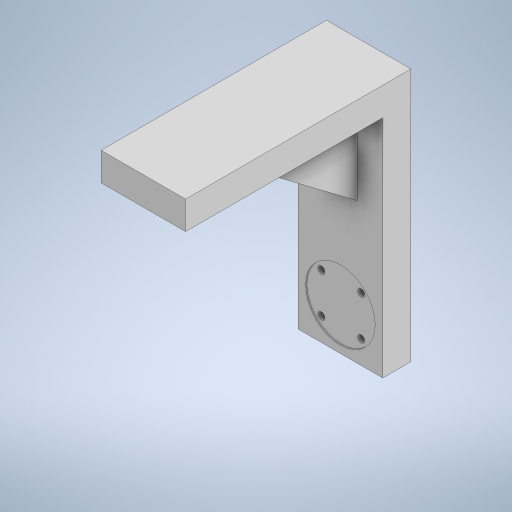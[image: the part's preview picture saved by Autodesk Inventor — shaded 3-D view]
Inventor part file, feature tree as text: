
AUTODESK INVENTOR PART (.ipt)
format: ipt  version: 2024 (Build 280153000, 153)  size: 284,160 bytes
history: native  units: in
note: dims shown in document units (in); Inventor stores cm internally (conversion verified against a paired STEP export)
features: sketch x7, extrude x6, rib x1
ambient origin geometry x8: Origin, YZ Plane, XZ Plane, XY Plane, X Axis, Y Axis, Z Axis, Center Point
bodies: Body1 (feature_tree)
feature tree (14):
  extrude  "Extrusion8"  Depth=1.9685in TaperAngle=0.0deg
  extrude  "Extrusion10"  Depth=3.0in
  extrude  "Extrusion11"  Depth=1.0in TaperAngle=0.0deg
  extrude  "Extrusion12"  Depth=7.0in TaperAngle=0.0deg
  rib  "Rib2"
  extrude  "Extrusion14"  [1 undecoded]
  extrude  "Extrusion15"  Depth=1.0in
  sketch  "Sketch7"  dims[d33=2.463in d34=1.9685in d35=0.0in]
  sketch  "Sketch9"  dims[d43=3.0in d44=3.0in]
  sketch  "Sketch10"  dims[d45=1.0in d46=0.0in d47=6.0in d48=0.0in]
  sketch  "Sketch11"  dims[d49=1.0in d50=7.0in d51=0.0in]
  sketch  "Sketch14"  dims[d70=3.0in d71=-0.3642in]
  sketch  "Sketch16"  dims[d72=4.0in]
  sketch  "Sketch17"  dims[d73=0.0394in d74=1.1811in d75=0.0in d76=0.0in d77=0.0394in d78=0.0394in d89=0.25in d90=0.707in d91=0.707in d92=1.5748in d94=360.0deg d96=1.0in d97=0.0in d98=0.0in d99=2.0in d100=0.0in]
note: 1 required parameter value undecoded (feature->parameter linkage not recoverable at this tier; creation-order binding heuristic only, values carry confidence <= 0.55)
